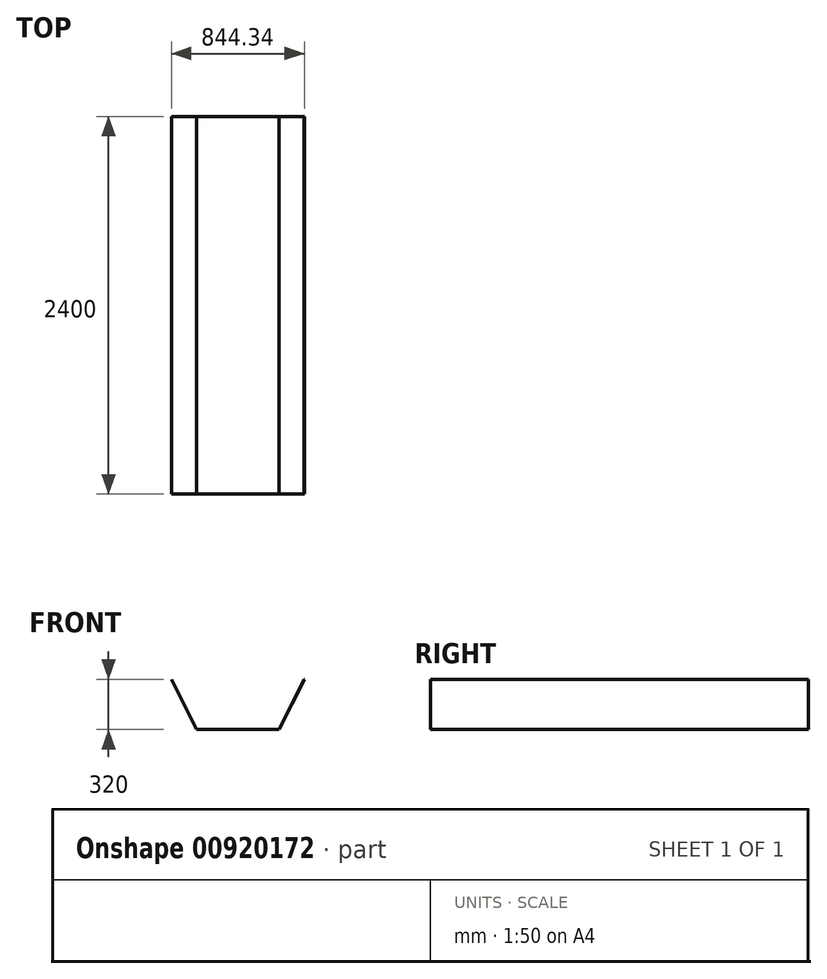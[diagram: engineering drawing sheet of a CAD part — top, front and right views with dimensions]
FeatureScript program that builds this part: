
annotation { "Feature Type Name" : "Feature", "Feature Type Description" : "" }
export const myFeature = defineFeature(function(context is Context, id is Id, definition is map)
    precondition{}
    {
        {
            var Q0;
            Q0=qCreatedBy(makeId("Front.planeOp"),FACE);
            var sketch = newSketch(context, id + "F0", { "sketchPlane" : qUnion([Q0])});
            skLineSegment(sketch, "E0.0", {"start": v(-388.22, 157.92) * mm, "end": v(-239.02, -140.48) * mm});
            skLineSegment(sketch, "E1.0", {"start": v(-221.13, -151.53) * mm, "end": v(276.9, -151.53) * mm});
            skLineSegment(sketch, "E2.0", {"start": v(443.98, 157.92) * mm, "end": v(294.78, -140.48) * mm});
            skLineSegment(sketch, "E3", {"start": v(-388.22, 157.92) * mm, "end": v(-392.7, 166.87) * mm});
            skLineSegment(sketch, "E4", {"start": v(443.98, 157.92) * mm, "end": v(448.45, 166.87) * mm});
            skLineSegment(sketch, "E5", {"start": v(-239.02, -140.48) * mm, "end": v(-233.5, -151.53) * mm});
            skLineSegment(sketch, "E6", {"start": v(-221.13, -151.53) * mm, "end": v(-233.5, -151.53) * mm});
            skLineSegment(sketch, "E7", {"start": v(276.9, -151.53) * mm, "end": v(289.25, -151.53) * mm});
            skLineSegment(sketch, "E8", {"start": v(294.78, -140.48) * mm, "end": v(289.25, -151.53) * mm});
            skLineSegment(sketch, "E9", {"start": v(-392.7, 166.87) * mm, "end": v(-394.3, 166.87) * mm});
            skLineSegment(sketch, "E10", {"start": v(-394.3, 166.87) * mm, "end": v(-234.3, -153.13) * mm});
            skLineSegment(sketch, "E11", {"start": v(448.45, 166.87) * mm, "end": v(450.05, 166.87) * mm});
            skLineSegment(sketch, "E12", {"start": v(450.05, 166.87) * mm, "end": v(290.05, -153.13) * mm});
            skLineSegment(sketch, "E13", {"start": v(290.05, -153.13) * mm, "end": v(-234.3, -153.13) * mm});
            skSolve(sketch);
        }
        {
            var Q0;
            Q0 = qSketchRegion(id + "F0", true);
            extrude(context, id + "F1", {"entities" : qUnion([Q0]), "depth" : 2400 * mm, "offsetDistance" : 25 * mm});
        }
    });
